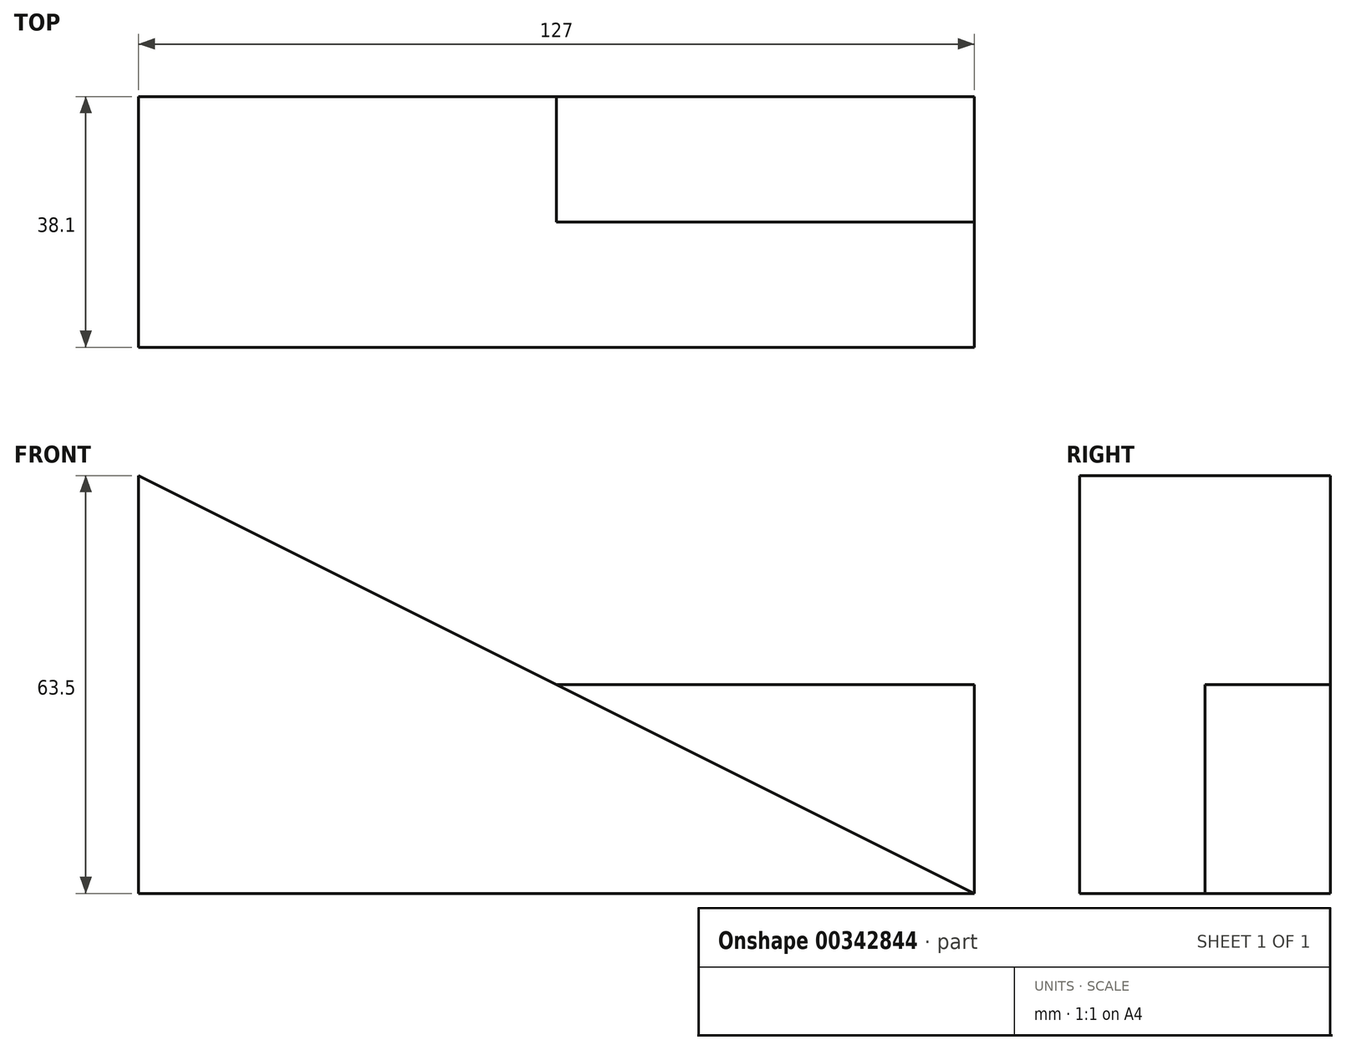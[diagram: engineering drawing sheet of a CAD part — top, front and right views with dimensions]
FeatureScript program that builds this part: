
annotation { "Feature Type Name" : "Feature", "Feature Type Description" : "" }
export const myFeature = defineFeature(function(context is Context, id is Id, definition is map)
    precondition{}
    {
        {
            var Q0;
            Q0=qCreatedBy(makeId("Front.planeOp"),FACE);
            var sketch = newSketch(context, id + "F0", { "sketchPlane" : qUnion([Q0])});
            skLineSegment(sketch, "E0.bottom", {"start": v(-63.5, -31.75) * mm, "end": v(63.5, -31.75) * mm});
            skLineSegment(sketch, "E0.left", {"start": v(-63.5, -31.75) * mm, "end": v(-63.5, 31.75) * mm});
            skPoint(sketch, "E0.middle", {"position": v(0, 0) * mm});
            skLineSegment(sketch, "E1", {"start": v(-63.5, 31.75) * mm, "end": v(63.5, -31.75) * mm});
            skPoint(sketch, "E0.right.end.orphan", {"position": v(63.5, 31.75) * mm});
            skLineSegment(sketch, "E2", {"start": v(63.5, -31.75) * mm, "end": v(63.5, 0) * mm});
            skLineSegment(sketch, "E3", {"start": v(63.5, 0) * mm, "end": v(0, 0) * mm});
            skSolve(sketch);
        }
        {
            var Q0;
            {var subQ0=sQuery(id+"F0.wireOp",EDGE,"E0.bottom");Q0=makeQuery(id+"F0.imprint","IMPRINT",FACE,{"disambiguationData":[TD([[makeQuery(id+"F0.imprint","IMPRINT",EDGE,{"derivedFrom":subQ0}),1.0]])]});}
            extrude(context, id + "F1", {"entities" : qUnion([Q0]), "depth" : 38.1 * mm});
        }
        {
            var Q0;
            Q0 = qSketchRegion(id + "F0", true);
            extrude(context, id + "F2", {"entities" : qUnion([Q0]), "operationType" : NewBodyOperationType.ADD, "depth" : 19.05 * mm});
        }
    });
